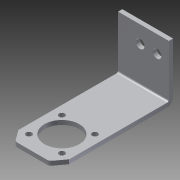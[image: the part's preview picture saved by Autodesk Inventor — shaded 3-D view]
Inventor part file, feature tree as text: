
AUTODESK INVENTOR PART (.ipt)
format: ipt  version: 2013 (Build 170138000, 138)  size: 257,536 bytes
history: native  units: in
note: dims shown in document units (in); Inventor stores cm internally (conversion verified against a paired STEP export)
features: sketch x5, other x5, sheet_metal_op x4, extrude x2, reference x2
ambient origin geometry x8: Origin, YZ Plane, XZ Plane, XY Plane, X Axis, Y Axis, Z Axis, Center Point
bodies: Solid1 (feature_tree)
feature tree (18):
  sheet_metal_op  "Face1"
  sheet_metal_op  "Flange2"
  extrude  "Extrusion1"  Depth=0.125in
  extrude  "Extrusion3"  Depth=0.25in
  sketch  "Sketch1"  dims[d1=0.125in d52=0.125in]
  other  "Plate1"
  sketch  "Sketch9"  dims[d53=0.0625in d54=0.25in]
  other  "Plate6"
  sheet_metal_op  "Bend5"
  sheet_metal_op  "Corner2"
  sketch  "Sketch10"  dims[d55=0.125in]
  sketch  "Sketch12"  dims[d56=1.475in d57=90.0deg d58=0.05in]
  sketch  "Sketch13"  dims[d59=0.5in d60=0.125in d61=0.125in d62=0.206in d63=0.0in d64=1.0in d65=1.625in d66=1.0in d67=0.25in d70=3.4105in d71=0.125in d72=0.375in d73=0.169in d74=1.028in d75=0.9858in d76=90.0deg d77=0.251in d78=90.0deg d79=3.5in d80=1.75in d81=3.5in d82=2.8497in d83=1.75in d84=0.0372in d85=0.625in d86=0.3162in d87=1.2628in d88=0.2411in d89=1.2628in d90=0.8211in d91=1.75in d92=0.9226in d93=2.2372in d94=1.0241in d95=2.2372in d96=1.6041in d97=2.875in d98=2.1242in d99=2222.0in d100=0.0in d101=0.125in d102=0.0in d0=0.0625in d2=0.0312in d3=0.0625in d4=0.125in d5=0.0in]
  reference  "Reference1"
  reference  "Reference2"
  other  "Cut4"
  other  "Definition1"
  other  "Cut1"
